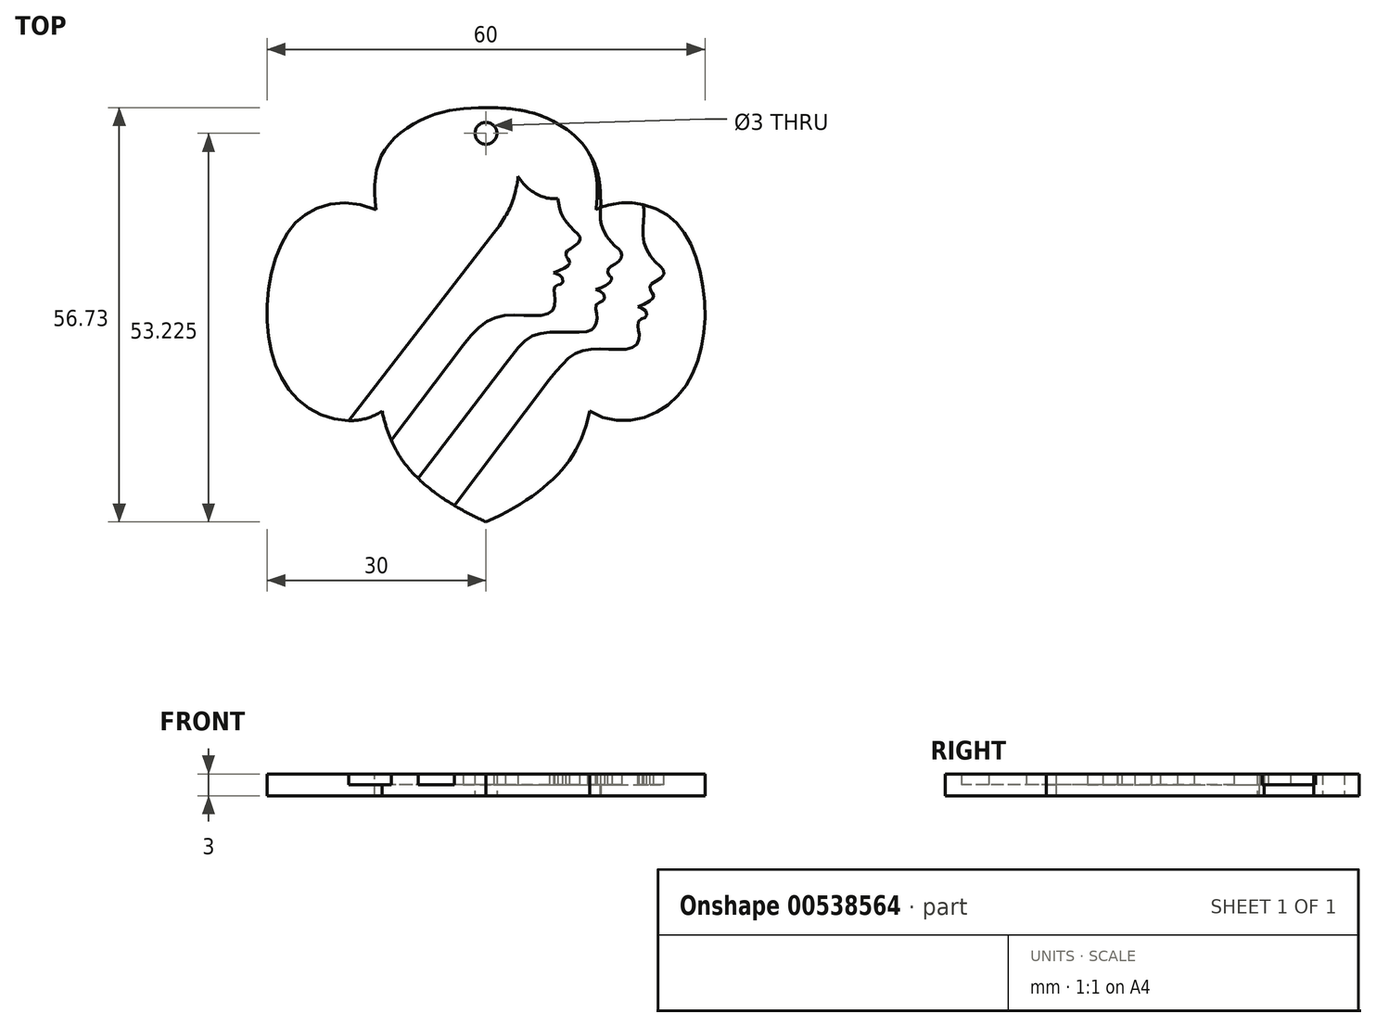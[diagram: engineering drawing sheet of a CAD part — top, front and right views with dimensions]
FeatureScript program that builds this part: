
annotation { "Feature Type Name" : "Feature", "Feature Type Description" : "" }
export const myFeature = defineFeature(function(context is Context, id is Id, definition is map)
    precondition{}
    {
        {
            var Q0;
            Q0=qCreatedBy(makeId("Top.planeOp"),FACE);
            var sketch = newSketch(context, id + "F0", { "sketchPlane" : qUnion([Q0])});
            skFitSpline(sketch, "E0", {"points": [v(-7.54, 7.43) * mm, v(-11.88, 7.37) * mm, v(-14.12, 4.84) * mm, v(-15, 0) * mm, v(-13.93, -4.24) * mm, v(-11.13, -6.7) * mm, v(-7.12, -6.38) * mm], "startDerivative": vector(-26.81, 12.19) * mm, "endDerivative": vector(21.6, 14.73) * mm});
            skFitSpline(sketch, "E1", {"points": [v(-7.54, 7.43) * mm, v(-6.99, 11.4) * mm, v(-3.73, 13.86) * mm, v(0, 14.4) * mm], "startDerivative": vector(-1.56, 13.23) * mm, "endDerivative": vector(12.02, 0) * mm});
            skFitSpline(sketch, "E2", {"points": [v(-7.12, -6.38) * mm, v(-4.93, -10.7) * mm, v(0, -13.96) * mm], "startDerivative": vector(2.76, -12.27) * mm, "endDerivative": vector(11.51, -5.2) * mm});
            skFitSpline(sketch, "E3.MirrorCS", {"points": [v(7.12, -6.38) * mm, v(4.93, -10.7) * mm, v(0, -13.96) * mm], "startDerivative": vector(-2.76, -12.27) * mm, "endDerivative": vector(-11.51, -5.2) * mm});
            skFitSpline(sketch, "E4.MirrorCS", {"points": [v(7.54, 7.43) * mm, v(6.99, 11.4) * mm, v(3.73, 13.86) * mm, v(0, 14.4) * mm], "startDerivative": vector(1.56, 13.23) * mm, "endDerivative": vector(-12.02, 0) * mm});
            skFitSpline(sketch, "E5.MirrorCS", {"points": [v(7.54, 7.43) * mm, v(11.88, 7.37) * mm, v(14.12, 4.84) * mm, v(15, 0) * mm, v(13.93, -4.24) * mm, v(11.13, -6.7) * mm, v(7.12, -6.38) * mm], "startDerivative": vector(26.81, 12.19) * mm, "endDerivative": vector(-21.6, 14.73) * mm});
            skLineSegment(sketch, "E6", {"start": v(-9.4, -7.03) * mm, "end": v(0.55, 5.84) * mm});
            skLineSegment(sketch, "E7", {"start": v(-6.49, -8.38) * mm, "end": v(-1.55, -1.86) * mm});
            skLineSegment(sketch, "E8", {"start": v(-4.64, -10.98) * mm, "end": v(1.34, -3.16) * mm});
            skLineSegment(sketch, "E9", {"start": v(-2.18, -12.83) * mm, "end": v(4.36, -4.21) * mm});
            skFitSpline(sketch, "E10", {"points": [v(0.55, 5.84) * mm, v(2.2, 9.7) * mm], "startDerivative": vector(2.92, 3.62) * mm, "endDerivative": vector(0.57, 4.77) * mm});
            skFitSpline(sketch, "E11", {"points": [v(2.2, 9.7) * mm, v(4.93, 8.18) * mm], "startDerivative": vector(1.82, -3.06) * mm, "endDerivative": vector(2.72, 0.45) * mm});
            skFitSpline(sketch, "E12", {"points": [v(-1.55, -1.86) * mm, v(1.02, 0.12) * mm, v(3.66, 0.18) * mm, v(4.65, 0.65) * mm, v(4.7, 1.6) * mm, v(4.7, 2.06) * mm, v(4.96, 2.28) * mm, v(5.18, 2.34) * mm, v(5.25, 2.73) * mm, v(4.86, 3.03) * mm, v(4.65, 3.08) * mm], "startDerivative": vector(12.23, 17.06) * mm, "endDerivative": vector(-3.7, 0.6) * mm});
            skFitSpline(sketch, "E13", {"points": [v(4.65, 3.08) * mm, v(5.6, 3.58) * mm, v(5.75, 3.85) * mm, v(5.6, 4.06) * mm, v(5.48, 4.47) * mm, v(5.75, 4.73) * mm, v(6.38, 5.22) * mm, v(6.41, 5.6) * mm, v(5.77, 6.25) * mm, v(5.13, 7.24) * mm, v(4.93, 8.18) * mm], "startDerivative": vector(8.75, 3.54) * mm, "endDerivative": vector(-0.95, 7.61) * mm});
            skFitSpline(sketch, "E14", {"points": [v(1.34, -3.16) * mm, v(3.02, -1.32) * mm, v(5.14, -0.96) * mm, v(7.05, -0.9) * mm, v(7.42, -0.63) * mm, v(7.62, -0.08) * mm, v(7.54, 0.47) * mm, v(7.55, 0.93) * mm, v(7.95, 1.16) * mm, v(8.11, 1.36) * mm, v(8.03, 1.68) * mm, v(7.51, 1.95) * mm], "startDerivative": vector(10.49, 13.37) * mm, "endDerivative": vector(-7.48, 2.84) * mm});
            skFitSpline(sketch, "E15", {"points": [v(7.51, 1.95) * mm, v(8.45, 2.4) * mm, v(8.62, 2.72) * mm, v(8.45, 2.91) * mm, v(8.34, 3.31) * mm, v(8.92, 3.74) * mm, v(9.3, 4.18) * mm, v(9.22, 4.57) * mm, v(8.72, 5.04) * mm, v(7.91, 6.36) * mm, v(7.85, 7.56) * mm, v(7.64, 9.94) * mm, v(6.99, 11.4) * mm], "startDerivative": vector(11.75, 4.35) * mm, "endDerivative": vector(-6.59, 11.31) * mm});
            skFitSpline(sketch, "E16", {"points": [v(4.36, -4.21) * mm, v(6.18, -2.4) * mm, v(8.4, -2.13) * mm, v(10.17, -1.95) * mm, v(10.5, -1.21) * mm, v(10.4, -0.64) * mm, v(10.56, -0.1) * mm, v(10.96, 0.06) * mm, v(10.95, 0.48) * mm, v(10.4, 0.76) * mm], "startDerivative": vector(10.47, 12.54) * mm, "endDerivative": vector(-7.53, 2.16) * mm});
            skFitSpline(sketch, "E17", {"points": [v(10.4, 0.76) * mm, v(11.37, 1.27) * mm, v(11.49, 1.54) * mm, v(11.37, 1.7) * mm, v(11.23, 2.07) * mm, v(11.33, 2.32) * mm, v(12.1, 2.84) * mm, v(12.15, 3.28) * mm, v(11.37, 4.1) * mm, v(10.75, 5.58) * mm, v(10.82, 7.03) * mm, v(10.76, 7.77) * mm], "startDerivative": vector(10.34, 4.27) * mm, "endDerivative": vector(-1.4, 7.4) * mm});
            skCircle(sketch, "E18", {"center": v(0, 12.65) * mm, "radius": 0.75 * mm});
            skSolve(sketch);
        }
        {
            var Q0;
            Q0 = qSketchRegion(id + "F0", true);
            extrude(context, id + "F1", {"entities" : qUnion([Q0]), "depth" : 0.75 * mm, "offsetDistance" : 25 * mm});
        }
        {
            var Q0;
            {var subQ2=sQuery(id+"F0.wireOp",EDGE,"E1");Q0=makeQuery(id+"F0.imprint","IMPRINT",FACE,{"disambiguationData":[TD([[makeQuery(id+"F0.imprint","IMPRINT",EDGE,{"derivedFrom":subQ2}),-1.0]])]});}
            var Q1;
            {var subQ1=sQuery(id+"F0.wireOp",EDGE,"E3.MirrorCS");Q1=makeQuery(id+"F0.imprint","IMPRINT",FACE,{"disambiguationData":[TD([[makeQuery(id+"F0.imprint","IMPRINT",EDGE,{"derivedFrom":subQ1}),-1.0]])]});}
            extrude(context, id + "F2", {"entities" : qUnion([Q0, Q1]), "operationType" : NewBodyOperationType.ADD, "depth" : 1.5 * mm, "offsetDistance" : 25 * mm});
        }
        {
            var Q0;
            Q0=makeQuery(id+"F0.imprint","IMPRINT",FACE,{"disambiguationData":[TD([[makeQuery(id+"F0.imprint","IMPRINT",EDGE,{"derivedFrom":sQuery(id+"F0.wireOp",EDGE,"E18")}),1.0]])]});
            extrude(context, id + "F3", {"entities" : qUnion([Q0]), "operationType" : NewBodyOperationType.REMOVE, "endBound" : BoundingType.THROUGH_ALL, "depth" : 25 * mm, "offsetDistance" : 25 * mm});
        }
        {
            var Q0;
            Q0=makeQuery(id+"F1.opExtrude","SWEPT_BODY",BODY,{"disambiguationData":[OSD([sQuery(id+"F0.wireOp",EDGE,"E0"),sQuery(id+"F0.wireOp",EDGE,"E1"),sQuery(id+"F0.wireOp",EDGE,"E2"),sQuery(id+"F0.wireOp",EDGE,"E3.MirrorCS"),sQuery(id+"F0.wireOp",EDGE,"E4.MirrorCS"),sQuery(id+"F0.wireOp",EDGE,"E5.MirrorCS"),sQuery(id+"F0.wireOp",EDGE,"E15"),sQuery(id+"F0.wireOp",EDGE,"E18")])]});
            var Q1;
            Q1=qCreatedBy(makeId("Origin.pointOp"),VERTEX);
            transform(context, id + "F4", {"entities" : qUnion([Q0]), "transformType" : TransformType.SCALE_UNIFORMLY, "scale" : 2, "scalePoint" : qUnion([Q1]), "makeCopy" : false});
        }
    });
